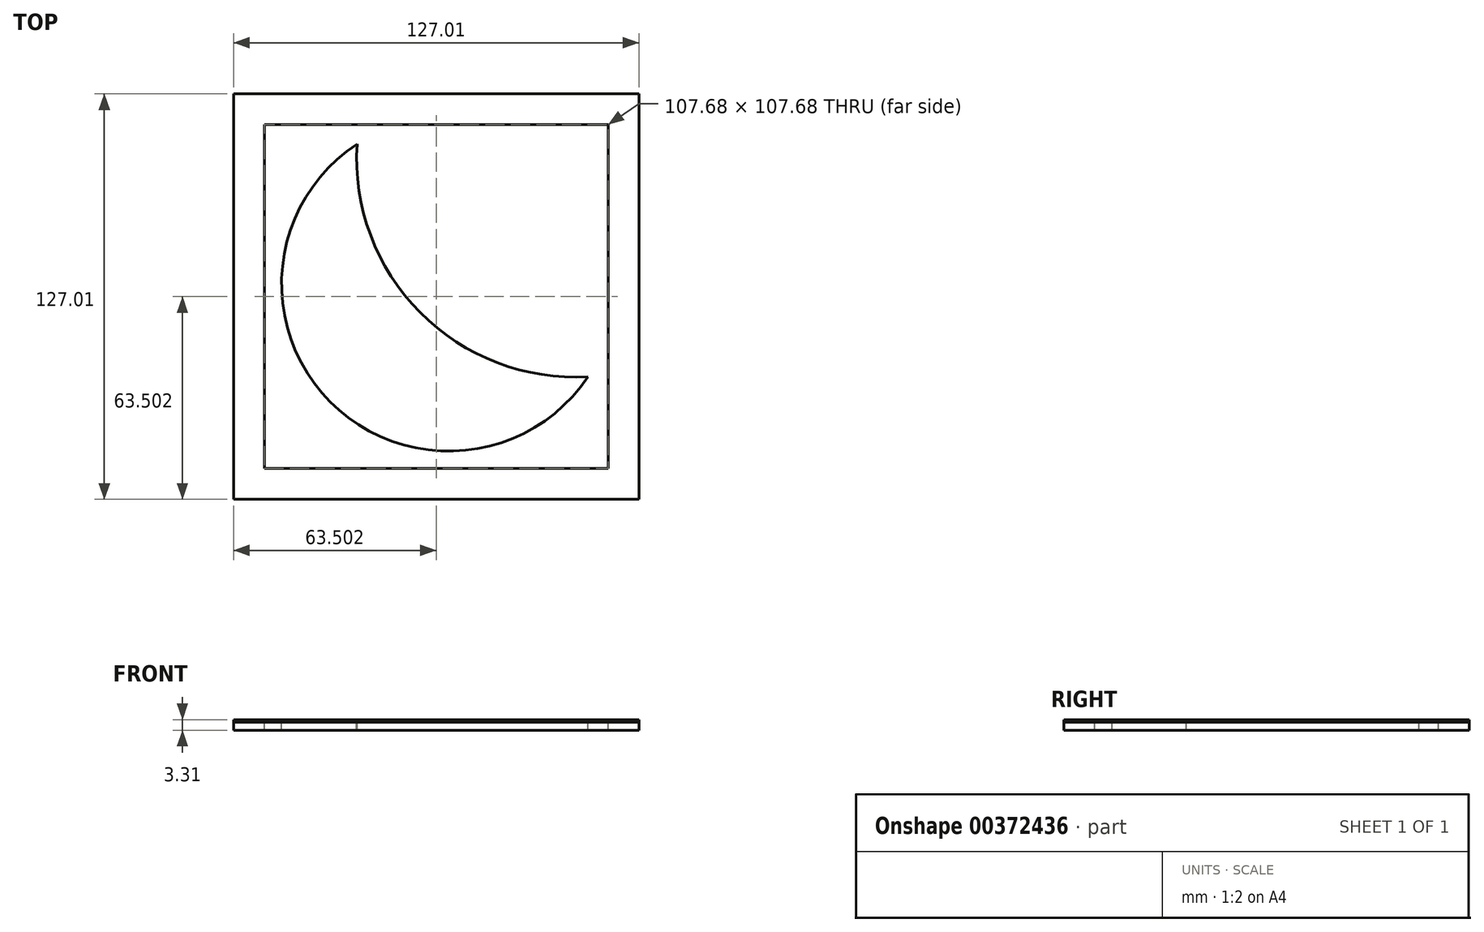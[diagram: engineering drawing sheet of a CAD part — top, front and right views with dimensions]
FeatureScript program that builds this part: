
annotation { "Feature Type Name" : "Feature", "Feature Type Description" : "" }
export const myFeature = defineFeature(function(context is Context, id is Id, definition is map)
    precondition{}
    {
        {
            var Q0;
            Q0=qCreatedBy(makeId("Top.planeOp"),FACE);
            var sketch = newSketch(context, id + "F0", { "sketchPlane" : qUnion([Q0])});
            skLineSegment(sketch, "E0.bottom", {"start": v(25.3, 25.86) * mm, "end": v(142.14, 25.86) * mm});
            skLineSegment(sketch, "E0.top", {"start": v(25.3, 142.7) * mm, "end": v(142.14, 142.7) * mm});
            skLineSegment(sketch, "E0.left", {"start": v(25.3, 25.86) * mm, "end": v(25.3, 142.7) * mm});
            skLineSegment(sketch, "E0.right", {"start": v(142.14, 25.86) * mm, "end": v(142.14, 142.7) * mm});
            skArc(sketch, "E1", {"start": v(60.92, 128.24) * mm, "mid": v(79.07, 79.7) * mm, "end": v(127.46, 61.2) * mm});
            skArc(sketch, "E2", {"start": v(60.92, 128.24) * mm, "mid": v(53.14, 53.97) * mm, "end": v(127.46, 61.2) * mm});
            skLineSegment(sketch, "E3.bottom", {"start": v(34.2, 34.75) * mm, "end": v(133.25, 34.75) * mm});
            skLineSegment(sketch, "E3.top", {"start": v(34.2, 133.8) * mm, "end": v(133.25, 133.8) * mm});
            skLineSegment(sketch, "E3.left", {"start": v(34.2, 34.75) * mm, "end": v(34.2, 133.8) * mm});
            skLineSegment(sketch, "E3.right", {"start": v(133.25, 34.75) * mm, "end": v(133.25, 133.8) * mm});
            skLineSegment(sketch, "E4", {"start": v(34.2, 84.28) * mm, "end": v(25.3, 84.28) * mm, "construction": true});
            skSolve(sketch);
        }
        {
            var Q0;
            Q0=makeQuery(id+"F0.imprint","IMPRINT",FACE,{"disambiguationData":[TD([[makeQuery(id+"F0.imprint","IMPRINT",EDGE,{"derivedFrom":sQuery(id+"F0.wireOp",EDGE,"E1")}),-1.0]])]});
            var Q1;
            Q1=makeQuery(id+"F0.imprint","IMPRINT",FACE,{"disambiguationData":[TD([[makeQuery(id+"F0.imprint","IMPRINT",EDGE,{"derivedFrom":sQuery(id+"F0.wireOp",EDGE,"E0.bottom")}),1.0]])]});
            extrude(context, id + "F1", {"entities" : qUnion([Q0, Q1]), "oppositeDirection" : true, "depth" : 3.04 * mm});
        }
        {
            var Q0;
            Q0=makeQuery(id+"F1.opExtrude","SWEPT_BODY",BODY,{"disambiguationData":[OSD([sQuery(id+"F0.wireOp",EDGE,"E0.bottom"),sQuery(id+"F0.wireOp",EDGE,"E0.top"),sQuery(id+"F0.wireOp",EDGE,"E0.left"),sQuery(id+"F0.wireOp",EDGE,"E0.right"),sQuery(id+"F0.wireOp",EDGE,"E3.bottom"),sQuery(id+"F0.wireOp",EDGE,"E3.top"),sQuery(id+"F0.wireOp",EDGE,"E3.left"),sQuery(id+"F0.wireOp",EDGE,"E3.right")])]});
            var Q1;
            Q1=makeQuery(id+"F1.opExtrude","SWEPT_BODY",BODY,{"disambiguationData":[OSD([sQuery(id+"F0.wireOp",EDGE,"E1"),sQuery(id+"F0.wireOp",EDGE,"E2")])]});
            var Q2;
            Q2=qCreatedBy(makeId("Origin.pointOp"),VERTEX);
            transform(context, id + "F2", {"entities" : qUnion([Q0, Q1]), "transformType" : TransformType.SCALE_UNIFORMLY, "scale" : 1.09, "scalePoint" : qUnion([Q2]), "makeCopy" : false});
        }
        {
            var Q0;
            Q0=makeQuery(id+"F1.opExtrude","SWEPT_BODY",BODY,{"disambiguationData":[OSD([sQuery(id+"F0.wireOp",EDGE,"E0.bottom"),sQuery(id+"F0.wireOp",EDGE,"E0.top"),sQuery(id+"F0.wireOp",EDGE,"E0.left"),sQuery(id+"F0.wireOp",EDGE,"E0.right"),sQuery(id+"F0.wireOp",EDGE,"E3.bottom"),sQuery(id+"F0.wireOp",EDGE,"E3.top"),sQuery(id+"F0.wireOp",EDGE,"E3.left"),sQuery(id+"F0.wireOp",EDGE,"E3.right")])]});
            var Q1;
            Q1=makeQuery(id+"F1.opExtrude","SWEPT_BODY",BODY,{"disambiguationData":[OSD([sQuery(id+"F0.wireOp",EDGE,"E1"),sQuery(id+"F0.wireOp",EDGE,"E2")])]});
            var Q2;
            Q2=makeQuery(id+"F1.opExtrude","CAP_VERTEX",VERTEX,{"disambiguationData":[OSD([sQuery(id+"F0.wireOp",EDGE,"E0.bottom"),sQuery(id+"F0.wireOp",EDGE,"E0.left")])],"isStart":false});
            var Q3;
            Q3=qCreatedBy(makeId("Origin.pointOp"),VERTEX);
            transform(context, id + "F3", {"entities" : qUnion([Q0, Q1]), "transformType" : TransformType.TRANSLATION_ENTITY, "oppositeDirectionEntity" : false, "transformLine" : qUnion([Q2, Q3]), "makeCopy" : false});
        }
        {
            var Q0;
            Q0=qCreatedBy(makeId("Top.planeOp"),FACE);
            var sketch = newSketch(context, id + "F4", { "sketchPlane" : qUnion([Q0])});
            skLineSegment(sketch, "E5.bottom", {"start": v(0, 0) * mm, "end": v(127, 0) * mm});
            skLineSegment(sketch, "E5.top", {"start": v(0, 127) * mm, "end": v(127, 127) * mm});
            skLineSegment(sketch, "E5.left", {"start": v(0, 0) * mm, "end": v(0, 127) * mm});
            skLineSegment(sketch, "E5.right", {"start": v(127, 0) * mm, "end": v(127, 127) * mm});
            skSolve(sketch);
        }
        {
            var Q0;
            Q0 = qSketchRegion(id + "F4", true);
            extrude(context, id + "F5", {"entities" : qUnion([Q0]), "depth" : 2.54 * mm});
        }
    });
